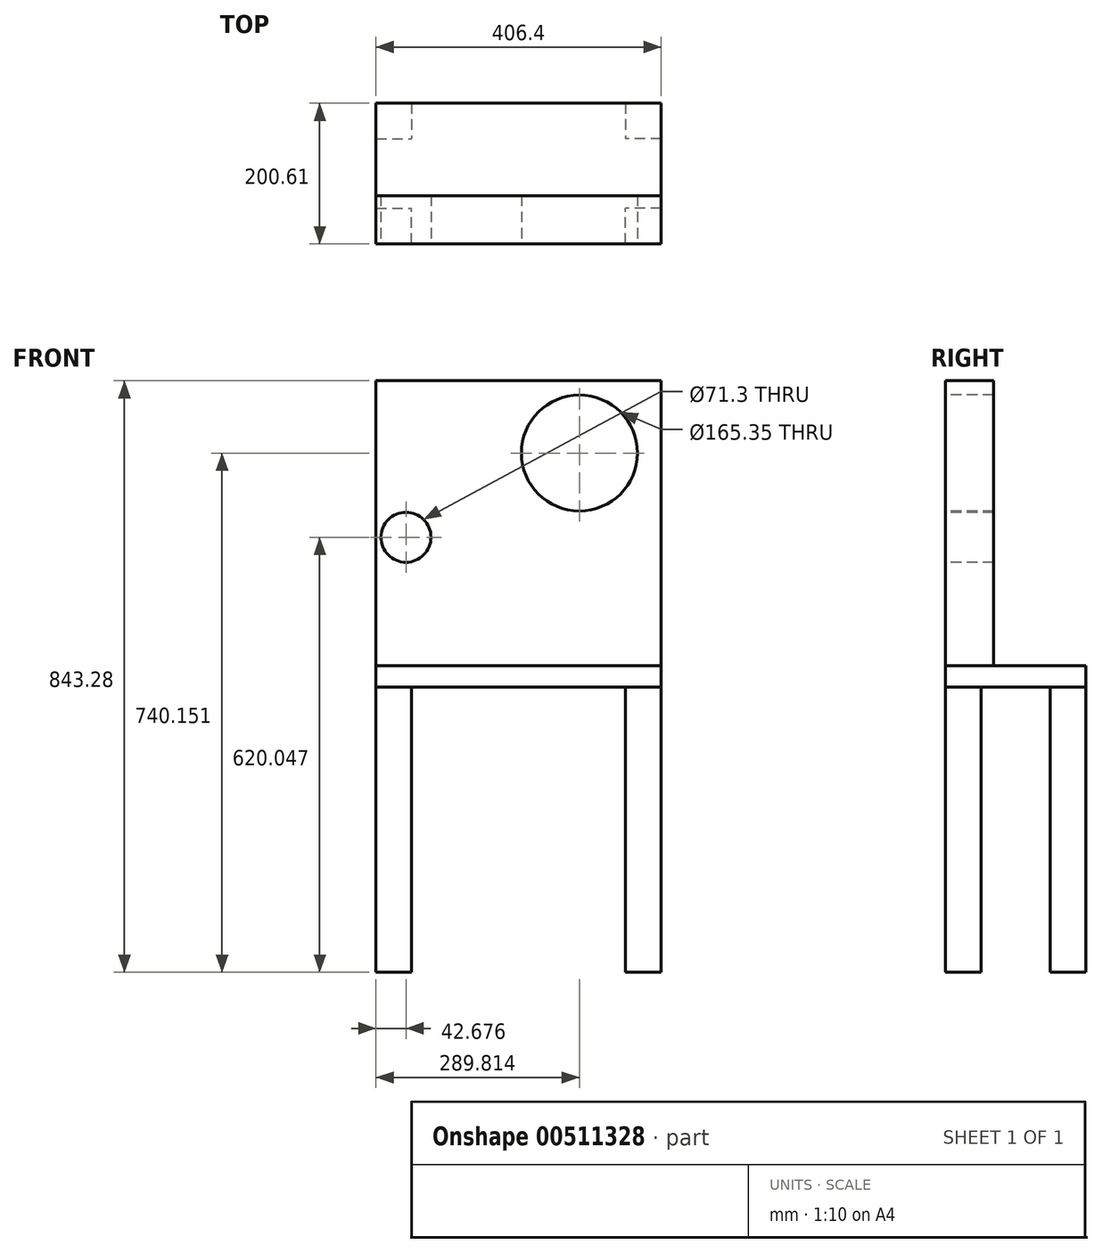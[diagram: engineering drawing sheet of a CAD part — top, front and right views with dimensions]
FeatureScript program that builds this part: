
annotation { "Feature Type Name" : "Feature", "Feature Type Description" : "" }
export const myFeature = defineFeature(function(context is Context, id is Id, definition is map)
    precondition{}
    {
        {
            var Q0;
            Q0=qCreatedBy(makeId("Top.planeOp"),FACE);
            var sketch = newSketch(context, id + "F0", { "sketchPlane" : qUnion([Q0])});
            skLineSegment(sketch, "E0.bottom", {"start": v(0, 0) * mm, "end": v(50.8, 0) * mm});
            skLineSegment(sketch, "E0.top", {"start": v(0, 50.8) * mm, "end": v(50.8, 50.8) * mm});
            skLineSegment(sketch, "E0.left", {"start": v(0, 0) * mm, "end": v(0, 50.8) * mm});
            skLineSegment(sketch, "E0.right", {"start": v(50.8, 0) * mm, "end": v(50.8, 50.8) * mm});
            skSolve(sketch);
        }
        {
            var Q0;
            Q0 = qSketchRegion(id + "F0", true);
            extrude(context, id + "F1", {"entities" : qUnion([Q0]), "depth" : 406.4 * mm});
        }
        {
            var Q0;
            Q0=makeQuery(id+"F1.opExtrude","CAP_FACE",FACE,{"disambiguationData":[OSD([sQuery(id+"F0.wireOp",EDGE,"E0.bottom"),sQuery(id+"F0.wireOp",EDGE,"E0.top"),sQuery(id+"F0.wireOp",EDGE,"E0.left"),sQuery(id+"F0.wireOp",EDGE,"E0.right")])],"isStart":false});
            var sketch = newSketch(context, id + "F2", { "sketchPlane" : qUnion([Q0])});
            skLineSegment(sketch, "E1", {"start": v(0, 0) * mm, "end": v(406.4, 0) * mm});
            skLineSegment(sketch, "E2", {"start": v(0, 0) * mm, "end": v(0, 200.61) * mm});
            skLineSegment(sketch, "E3", {"start": v(0, 200.61) * mm, "end": v(406.4, 200.61) * mm});
            skLineSegment(sketch, "E4", {"start": v(406.4, 200.61) * mm, "end": v(406.4, 0) * mm});
            skLineSegment(sketch, "E5", {"start": v(203.2, 200.61) * mm, "end": v(203.2, 0) * mm});
            skLineSegment(sketch, "E6", {"start": v(406.4, 100.3) * mm, "end": v(0, 100.3) * mm});
            skSolve(sketch);
        }
        {
            var Q0;
            Q0=sQuery(id+"F2.wireOp",EDGE,"E5");
            cPlane(context, id + "F3", {"entities" : qUnion([Q0]), "cplaneType" : CPlaneType.LINE_ANGLE, "offset" : 25.4 * mm, "angle" : 90 * degree, "width" : 152.4 * mm, "height" : 152.4 * mm});
        }
        {
            var Q0;
            Q0=sQuery(id+"F2.wireOp",EDGE,"E6");
            cPlane(context, id + "F4", {"entities" : qUnion([Q0]), "cplaneType" : CPlaneType.LINE_ANGLE, "offset" : 25.4 * mm, "angle" : 0 * degree, "width" : 152.4 * mm, "height" : 152.4 * mm});
        }
        {
            var Q0;
            Q0=makeQuery(id+"F1.opExtrude","SWEPT_BODY",BODY,{"disambiguationData":[OSD([sQuery(id+"F0.wireOp",EDGE,"E0.bottom"),sQuery(id+"F0.wireOp",EDGE,"E0.top"),sQuery(id+"F0.wireOp",EDGE,"E0.left"),sQuery(id+"F0.wireOp",EDGE,"E0.right")])]});
            var Q1;
            Q1=qCreatedBy(id+"F3.planeOp",FACE);
            mirror(context, id + "F5", {"entities" : qUnion([Q0]), "mirrorPlane" : qUnion([Q1])});
        }
        {
            var Q0;
            Q0=makeQuery(id+"F5.opPattern","COPY",BODY,{"derivedFrom":makeQuery(id+"F1.opExtrude","SWEPT_BODY",BODY,{"disambiguationData":[OSD([sQuery(id+"F0.wireOp",EDGE,"E0.bottom"),sQuery(id+"F0.wireOp",EDGE,"E0.top"),sQuery(id+"F0.wireOp",EDGE,"E0.left"),sQuery(id+"F0.wireOp",EDGE,"E0.right")])]}),"instanceName":"1"});
            var Q1;
            Q1=makeQuery(id+"F1.opExtrude","SWEPT_BODY",BODY,{"disambiguationData":[OSD([sQuery(id+"F0.wireOp",EDGE,"E0.bottom"),sQuery(id+"F0.wireOp",EDGE,"E0.top"),sQuery(id+"F0.wireOp",EDGE,"E0.left"),sQuery(id+"F0.wireOp",EDGE,"E0.right")])]});
            var Q2;
            Q2=qCreatedBy(id+"F4.planeOp",FACE);
            mirror(context, id + "F6", {"entities" : qUnion([Q0, Q1]), "mirrorPlane" : qUnion([Q2])});
        }
        {
            var Q0;
            Q0 = qSketchRegion(id + "F2", true);
            extrude(context, id + "F7", {"entities" : qUnion([Q0]), "depth" : 30.48 * mm});
        }
        {
            var Q0;
            Q0=makeQuery(id+"F7.opExtrude","CAP_FACE",FACE,{"disambiguationData":[OSD([sQuery(id+"F2.wireOp",EDGE,"E1"),sQuery(id+"F2.wireOp",EDGE,"E2"),sQuery(id+"F2.wireOp",EDGE,"E3"),sQuery(id+"F2.wireOp",EDGE,"E4")])],"isStart":false});
            var sketch = newSketch(context, id + "F8", { "sketchPlane" : qUnion([Q0])});
            skLineSegment(sketch, "E7.bottom", {"start": v(406.4, 0) * mm, "end": v(0, 0) * mm});
            skLineSegment(sketch, "E7.top", {"start": v(406.4, -172.04) * mm, "end": v(0, -172.04) * mm});
            skLineSegment(sketch, "E7.left", {"start": v(406.4, 0) * mm, "end": v(406.4, -172.04) * mm});
            skLineSegment(sketch, "E7.right", {"start": v(0, 0) * mm, "end": v(0, -172.04) * mm});
            skLineSegment(sketch, "E8", {"start": v(406.4, 68.87) * mm, "end": v(0, 68.87) * mm});
            skSolve(sketch);
        }
        {
            var Q0;
            {var subQ0=sQuery(id+"F8.wireOp",EDGE,"E7.bottom");Q0=makeQuery(id+"F8.imprint","IMPRINT",FACE,{"disambiguationData":[TD([[makeQuery(id+"F8.imprint","IMPRINT",EDGE,{"derivedFrom":subQ0}),1.0]])]});}
            extrude(context, id + "F9", {"entities" : qUnion([Q0]), "depth" : 406.4 * mm});
        }
        {
            var Q0;
            Q0=makeQuery(id+"F9.opExtrude","SWEPT_FACE",FACE,{"disambiguationData":[OSD([sQuery(id+"F8.wireOp",EDGE,"E7.bottom")])]});
            var sketch = newSketch(context, id + "F10", { "sketchPlane" : qUnion([Q0])});
            skCircle(sketch, "E9", {"center": v(289.81, 740.15) * mm, "radius": 82.67 * mm});
            skCircle(sketch, "E10", {"center": v(42.68, 620.05) * mm, "radius": 35.65 * mm});
            skSolve(sketch);
        }
        {
            var Q0;
            Q0=makeQuery(id+"F10.imprint","IMPRINT",FACE,{"disambiguationData":[TD([[makeQuery(id+"F10.imprint","IMPRINT",EDGE,{"derivedFrom":sQuery(id+"F10.wireOp",EDGE,"E10")}),1.0]])]});
            var Q1;
            Q1=makeQuery(id+"F10.imprint","IMPRINT",FACE,{"disambiguationData":[TD([[makeQuery(id+"F10.imprint","IMPRINT",EDGE,{"derivedFrom":sQuery(id+"F10.wireOp",EDGE,"E9")}),1.0]])]});
            extrude(context, id + "F11", {"entities" : qUnion([Q0, Q1]), "oppositeDirection" : true, "depth" : 193.04 * mm, "offsetDistance" : 25.4 * mm});
        }
        {
            var Q0;
            Q0=makeQuery(id+"F11.opExtrude","SWEPT_BODY",BODY,{"disambiguationData":[OSD([sQuery(id+"F10.wireOp",EDGE,"E9")])]});
            var Q1;
            Q1=makeQuery(id+"F11.opExtrude","SWEPT_BODY",BODY,{"disambiguationData":[OSD([sQuery(id+"F10.wireOp",EDGE,"E10")])]});
            var Q2;
            Q2=makeQuery(id+"F9.opExtrude","SWEPT_BODY",BODY,{"disambiguationData":[OSD([sQuery(id+"F2.wireOp",EDGE,"E2"),sQuery(id+"F2.wireOp",EDGE,"E4"),sQuery(id+"F8.wireOp",EDGE,"E7.bottom"),sQuery(id+"F8.wireOp",EDGE,"E8")])]});
            booleanBodies(context, id + "F12", {"operationType" : BooleanOperationType.SUBTRACTION, "tools" : qUnion([Q0, Q1]), "targets" : qUnion([Q2])});
        }
    });
